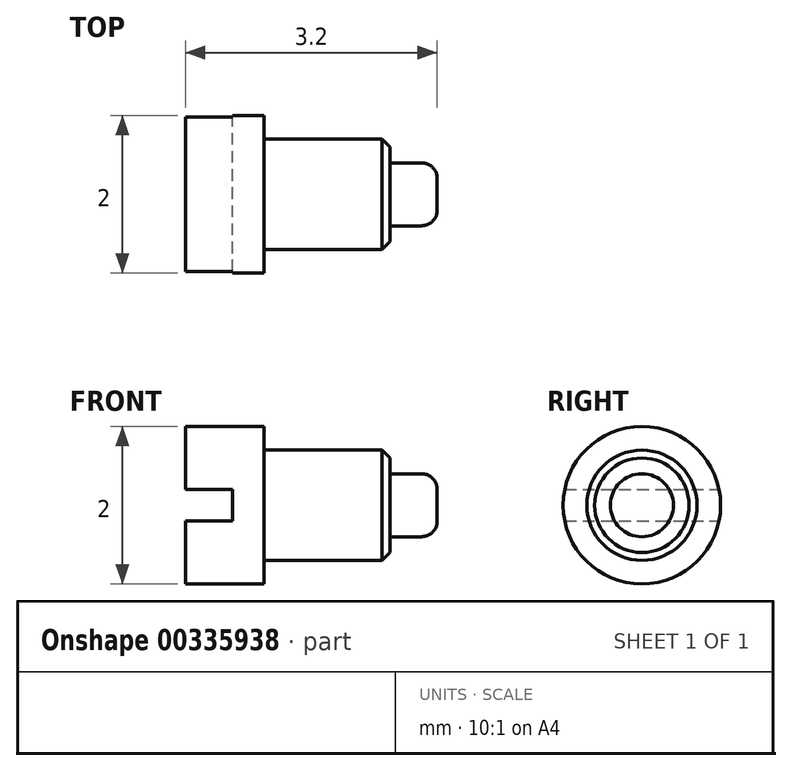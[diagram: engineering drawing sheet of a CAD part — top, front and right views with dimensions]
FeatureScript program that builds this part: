
annotation { "Feature Type Name" : "Feature", "Feature Type Description" : "" }
export const myFeature = defineFeature(function(context is Context, id is Id, definition is map)
    precondition{}
    {
        {
            var Q0;
            Q0=qCreatedBy(makeId("Front.planeOp"),FACE);
            var sketch = newSketch(context, id + "F0", { "sketchPlane" : qUnion([Q0])});
            skLineSegment(sketch, "E0.bottom", {"start": v(0, 1) * mm, "end": v(1, 1) * mm});
            skLineSegment(sketch, "E0.top", {"start": v(0, -1) * mm, "end": v(1, -1) * mm});
            skLineSegment(sketch, "E0.left", {"start": v(0, 1) * mm, "end": v(0, -1) * mm});
            skLineSegment(sketch, "E0.right", {"start": v(1, 1) * mm, "end": v(1, -1) * mm});
            skLineSegment(sketch, "E1.bottom", {"start": v(1, 0.7) * mm, "end": v(2.6, 0.7) * mm});
            skLineSegment(sketch, "E1.top", {"start": v(1, -0.7) * mm, "end": v(2.6, -0.7) * mm});
            skLineSegment(sketch, "E1.left", {"start": v(1, 0.7) * mm, "end": v(1, -0.7) * mm});
            skLineSegment(sketch, "E1.right", {"start": v(2.6, 0.7) * mm, "end": v(2.6, -0.7) * mm});
            skLineSegment(sketch, "E2.bottom", {"start": v(2.6, 0.4) * mm, "end": v(3, 0.4) * mm});
            skLineSegment(sketch, "E2.top", {"start": v(2.6, -0.4) * mm, "end": v(3, -0.4) * mm});
            skLineSegment(sketch, "E2.left", {"start": v(2.6, 0.4) * mm, "end": v(2.6, -0.4) * mm});
            skLineSegment(sketch, "E2.right", {"start": v(3.2, 0.2) * mm, "end": v(3.2, -0.2) * mm});
            skPoint(sketch, "E3", {"position": v(0, 0) * mm});
            skPoint(sketch, "E4", {"position": v(1, 0) * mm});
            skPoint(sketch, "E5", {"position": v(2.6, 0) * mm});
            skPoint(sketch, "E6", {"position": v(3.2, 0) * mm});
            skPoint(sketch, "E7.visualSharp", {"position": v(3.2, 0.4) * mm});
            skArc(sketch, "E7.filletArc", {"start": v(3.2, 0.2) * mm, "mid": v(3.14, 0.34) * mm, "end": v(3, 0.4) * mm});
            skPoint(sketch, "E8.visualSharp", {"position": v(3.2, -0.4) * mm});
            skArc(sketch, "E8.filletArc", {"start": v(3, -0.4) * mm, "mid": v(3.14, -0.34) * mm, "end": v(3.2, -0.2) * mm});
            skLineSegment(sketch, "E9", {"start": v(0, 0) * mm, "end": v(3.2, 0) * mm});
            skSolve(sketch);
        }
        {
            var Q0;
            {var subQ5=sQuery(id+"F0.wireOp",EDGE,"E0.bottom");Q0=makeQuery(id+"F0.imprint","IMPRINT",FACE,{"disambiguationData":[TD([[makeQuery(id+"F0.imprint","IMPRINT",EDGE,{"derivedFrom":subQ5}),-1.0]])]});}
            var Q1;
            {var subQ5=sQuery(id+"F0.wireOp",EDGE,"E1.bottom");Q1=makeQuery(id+"F0.imprint","IMPRINT",FACE,{"disambiguationData":[TD([[makeQuery(id+"F0.imprint","IMPRINT",EDGE,{"derivedFrom":subQ5}),-1.0]])]});}
            var Q2;
            {var subQ5=sQuery(id+"F0.wireOp",EDGE,"E2.bottom");Q2=makeQuery(id+"F0.imprint","IMPRINT",FACE,{"disambiguationData":[TD([[makeQuery(id+"F0.imprint","IMPRINT",EDGE,{"derivedFrom":subQ5}),-1.0]])]});}
            var Q3;
            Q3=sQuery(id+"F0.wireOp",EDGE,"E9");
            revolve(context, id + "F1", {"entities" : qUnion([Q0, Q1, Q2]), "axis" : qUnion([Q3]), "revolveType" : RevolveType.FULL});
        }
        {
            var Q0;
            Q0=makeQuery(id+"F1.opRevolve","SWEPT_EDGE",EDGE,{"disambiguationData":[OSD([sQuery(id+"F0.wireOp",EDGE,"E1.bottom"),sQuery(id+"F0.wireOp",EDGE,"E1.right")])]});
            chamfer(context, id + "F2", {"entities" : qUnion([Q0]), "width" : 0.1 * mm, "tangentPropagation" : true});
        }
        {
            var Q0;
            Q0=makeQuery(id+"F1.opRevolve","SWEPT_FACE",FACE,{"disambiguationData":[OSD([sQuery(id+"F0.wireOp",EDGE,"E0.left")])]});
            var sketch = newSketch(context, id + "F3", { "sketchPlane" : qUnion([Q0])});
            skLineSegment(sketch, "E10.bottom", {"start": v(1, -0.2) * mm, "end": v(-1, -0.2) * mm});
            skLineSegment(sketch, "E10.top", {"start": v(1, 0.2) * mm, "end": v(-1, 0.2) * mm});
            skLineSegment(sketch, "E10.left", {"start": v(1, -0.2) * mm, "end": v(1, 0.2) * mm});
            skLineSegment(sketch, "E10.right", {"start": v(-1, -0.2) * mm, "end": v(-1, 0.2) * mm});
            skPoint(sketch, "E10.middle", {"position": v(0, 0) * mm});
            skPoint(sketch, "E11", {"position": v(1, 0) * mm});
            skSolve(sketch);
        }
        {
            var Q0;
            Q0 = qSketchRegion(id + "F3", true);
            extrude(context, id + "F4", {"entities" : qUnion([Q0]), "operationType" : NewBodyOperationType.REMOVE, "oppositeDirection" : true, "depth" : 0.6 * mm});
        }
    });
